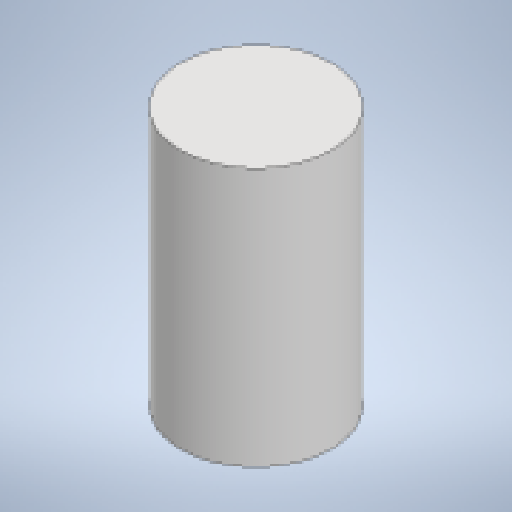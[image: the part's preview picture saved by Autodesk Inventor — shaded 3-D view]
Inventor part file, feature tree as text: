
AUTODESK INVENTOR PART (.ipt)
format: ipt  version: 2023 (Build 270158000, 158)  size: 129,024 bytes
history: native  units: in
note: dims shown in document units (in); Inventor stores cm internally (conversion verified against a paired STEP export)
features: revolve x1, sketch x1
ambient origin geometry x8: Origin, YZ Plane, XZ Plane, XY Plane, X Axis, Y Axis, Z Axis, Center Point
bodies: Solid1 (feature_tree)
feature tree (2):
  revolve  "Revolution1"  [1 undecoded]
  sketch  "Sketch1"  dims[d0=1.75in d1=6.0in d2=360.0deg d3=0.1875in d4=3.0in]
note: 1 required parameter value undecoded (feature->parameter linkage not recoverable at this tier; creation-order binding heuristic only, values carry confidence <= 0.55)
